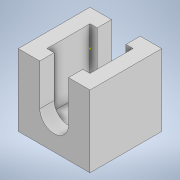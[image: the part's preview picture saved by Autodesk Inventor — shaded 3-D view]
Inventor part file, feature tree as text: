
AUTODESK INVENTOR PART (.ipt)
format: ipt  version: 2022 (Build 260153000, 153)  size: 116,736 bytes
history: native  units: in
note: dims shown in document units (in); Inventor stores cm internally (conversion verified against a paired STEP export)
features: sketch x7, extrude x2, shell x1
ambient origin geometry x8: Origin, YZ Plane, XZ Plane, XY Plane, X Axis, Y Axis, Z Axis, Center Point
bodies: Solid1 (feature_tree)
feature tree (10):
  extrude  "Extrusion1"  Depth=0.1969in
  shell  "Shell1"  Thickness=0.1969in
  extrude  "Extrusion3"  TaperAngle=0.0deg  [1 undecoded]
  sketch  "Sketch4"
  sketch  "Sketch5"
  sketch  "Sketch6"
  sketch  "Sketch7"
  sketch  "Sketch8"
  sketch  "Sketch1"  dims[d0=0.1969in d1=0.1969in d2=0.1969in d3=0.0in]
  sketch  "Sketch3"  dims[d4=0.0394in d8=0.0in d9=0.0in]
note: 1 required parameter value undecoded (feature->parameter linkage not recoverable at this tier; creation-order binding heuristic only, values carry confidence <= 0.55)
